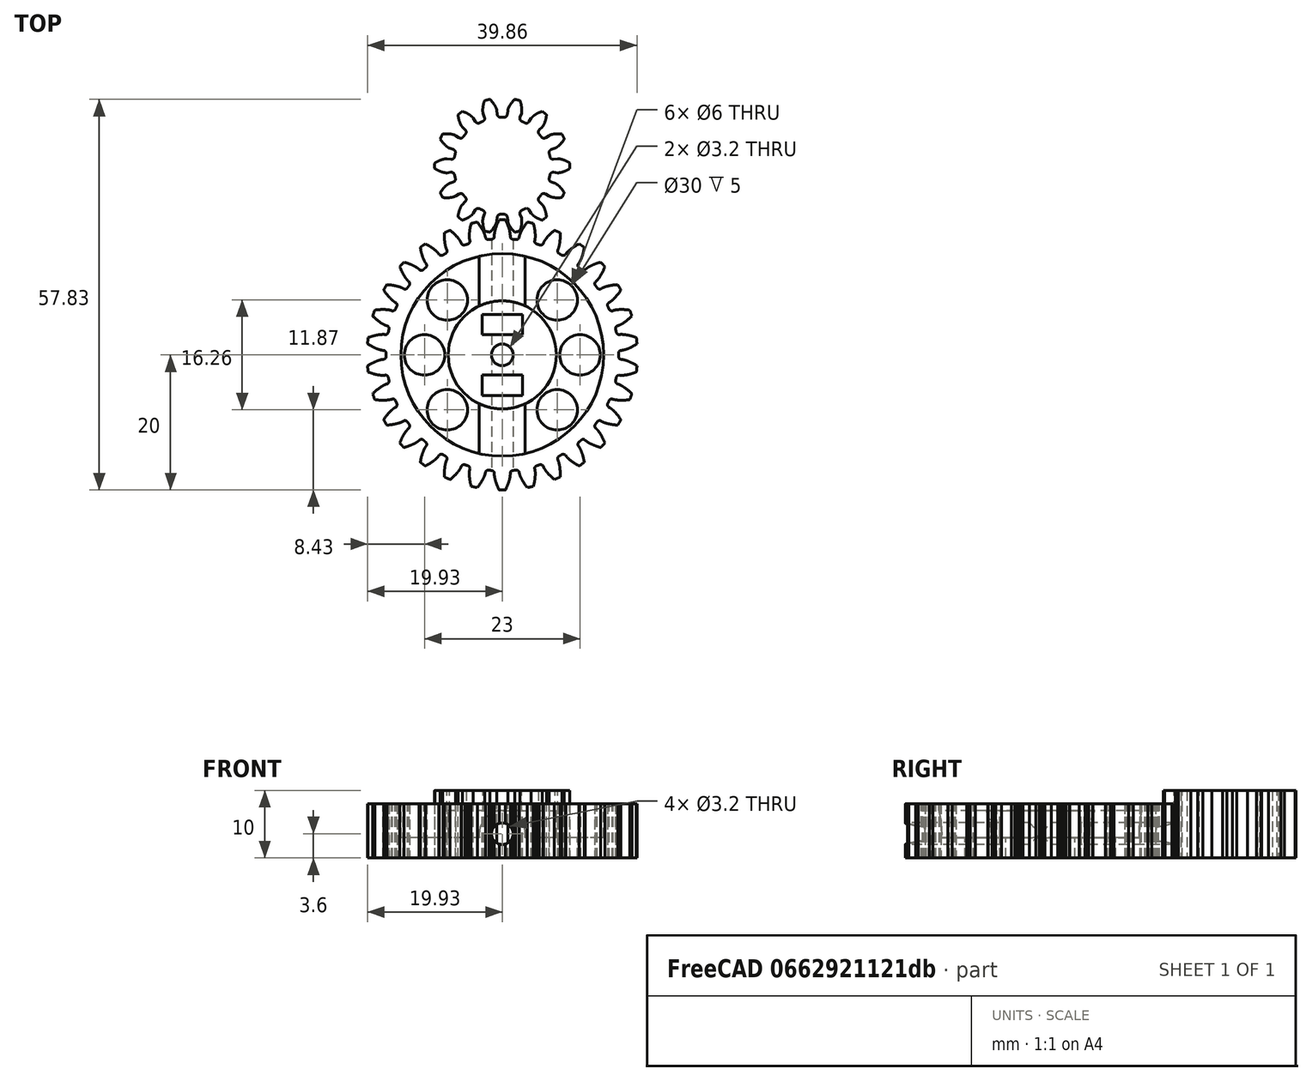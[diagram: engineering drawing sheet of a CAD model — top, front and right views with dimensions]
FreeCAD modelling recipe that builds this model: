
FCSTD DOCUMENT  (FreeCAD 0.14R3700 (Git))
Label: BigGear
License: CC-BY 3.0
LicenseURL: http://creativecommons.org/licenses/by/3.0/
objects: Part::Cylinder×11, Part::Cut×5, Part::Part2DObjectPython×2, PartDesign::Pad×2, Part::Box×2, Part::MultiFuse×2
note: 26 computed .brp shape members not serialized (recipe doc carries the construction recipe); baked Part::Feature solids carry a one-line shape summary decoded from their .brp

FEATURE [Part::Part2DObjectPython] InvoluteGear  # Draft 2D object (typed FeaturePython)
  Modules = 1.25
  NumberOfCurves = 0
  NumberOfTeeth = 30
  Placement = pos=(0,-28,0) rot=(0,0,1;0.10472rad)
  PressureAngle = 20
FEATURE [Part::Part2DObjectPython] InvoluteGear001  label="InvoluteGear14"  # Draft 2D object (typed FeaturePython)
  Modules = 1.25
  NumberOfCurves = 0
  NumberOfTeeth = 14
  PressureAngle = 20
FEATURE [PartDesign::Pad] Pad
  Length = 8
  Length2 = 100
  Placement = pos=(0,-28,0) rot=(0,0,1;0.10472rad)
  Sketch = -> InvoluteGear
  Type = 0
FEATURE [Part::Cylinder] Cylinder  label="DeltaCylinderCenter"
  Angle = 360
  Height = 5
  Placement = pos=(0,-28,3) rot=(0,0,1;0rad)
  Radius = 15
FEATURE [Part::Cylinder] Cylinder001
  Angle = 360
  Height = 10
  Placement = pos=(0,-28,0) rot=(0,0,1;0rad)
  Radius = 1.6
FEATURE [PartDesign::Pad] Pad001  label="SmallGear"
  Length = 10
  Length2 = 100
  Sketch = -> InvoluteGear001
  Type = 0
FEATURE [Part::Cylinder] Cylinder003  label="CylinderCenter"
  Angle = 360
  Height = 7
  Placement = pos=(0,-28,0) rot=(0,0,1;0rad)
  Radius = 8
FEATURE [Part::Cylinder] Cylinder005
  Angle = 360
  Height = 10
  Placement = pos=(11.5,-28,0) rot=(0,0,1;0rad)
  Radius = 3
FEATURE [Part::Cylinder] Cylinder006
  Angle = 360
  Height = 10
  Placement = pos=(-11.5,-28,0) rot=(0,0,1;0rad)
  Radius = 3
FEATURE [Part::Box] Box002  label="DeltaNutPocket1"
  Height = 10
  Length = 6
  Placement = pos=(-3,-25,0) rot=(0,0,1;0rad)
  Width = 3
FEATURE [Part::Box] Box003  label="DeltaNutPocket2"
  Height = 10
  Length = 6
  Placement = pos=(-3,-34,0) rot=(0,0,1;0rad)
  Width = 3
FEATURE [Part::Cylinder] Cylinder007  label="DeltaCylinderM3"
  Angle = 360
  Height = 50
  Placement = pos=(0,0,3.6) rot=(1,0,0;1.5708rad)
  Radius = 1.6
FEATURE [Part::Cylinder] Cylinder008
  Angle = 360
  Height = 10
  Placement = pos=(8.13,-19.87,0) rot=(0,0,1;0rad)
  Radius = 3
FEATURE [Part::Cylinder] Cylinder009
  Angle = 360
  Height = 10
  Placement = pos=(8.13,-36.13,0) rot=(0,0,1;0rad)
  Radius = 3
FEATURE [Part::Cylinder] Cylinder010
  Angle = 360
  Height = 10
  Placement = pos=(-8.13,-19.87,0) rot=(0,0,1;0rad)
  Radius = 3
FEATURE [Part::Cylinder] Cylinder011
  Angle = 360
  Height = 10
  Placement = pos=(-8.13,-36.13,0) rot=(0,0,1;0rad)
  Radius = 3
FEATURE [Part::MultiFuse] Fusion  label="DeltaFusionCylinders"
  Shapes = -> [Cylinder011,Cylinder001,Cylinder008,Cylinder009,Cylinder006,Cylinder005,Cylinder010]
FEATURE [Part::Cylinder] Cylinder012  label="CylinderReenforcingTunnel"
  Angle = 360
  Height = 32
  Placement = pos=(0,-12,3.6) rot=(1,0,0;1.5708rad)
  Radius = 3.4
FEATURE [Part::Cut] Cut
  Base = -> Pad
  Tool = -> Cylinder
FEATURE [Part::MultiFuse] Fusion001
  Shapes = -> [Cylinder003,Cut,Cylinder012]
FEATURE [Part::Cut] Cut001
  Base = -> Fusion001
  Tool = -> Fusion
FEATURE [Part::Cut] Cut002
  Base = -> Cut001
  Tool = -> Box002
FEATURE [Part::Cut] Cut003
  Base = -> Cut002
  Tool = -> Box003
FEATURE [Part::Cut] Cut004  label="BigGear"
  Base = -> Cut003
  Tool = -> Cylinder007
